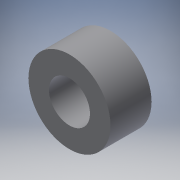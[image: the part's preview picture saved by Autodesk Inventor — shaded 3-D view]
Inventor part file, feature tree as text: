
AUTODESK INVENTOR PART (.ipt)
format: ipt  version: 2016 (Build 200138000, 138)  size: 95,232 bytes
history: native  units: in
note: dims shown in document units (in); Inventor stores cm internally (conversion verified against a paired STEP export)
features: extrude x1, sketch x1
ambient origin geometry x8: Origin, YZ Plane, XZ Plane, XY Plane, X Axis, Y Axis, Z Axis, Center Point
bodies: Solid1 (feature_tree)
feature tree (2):
  extrude  "Extrusion1"  Depth=0.125in
  sketch  "Sketch1"  dims[d0=0.25in d1=0.125in d2=0.25in d3=0.0in]
